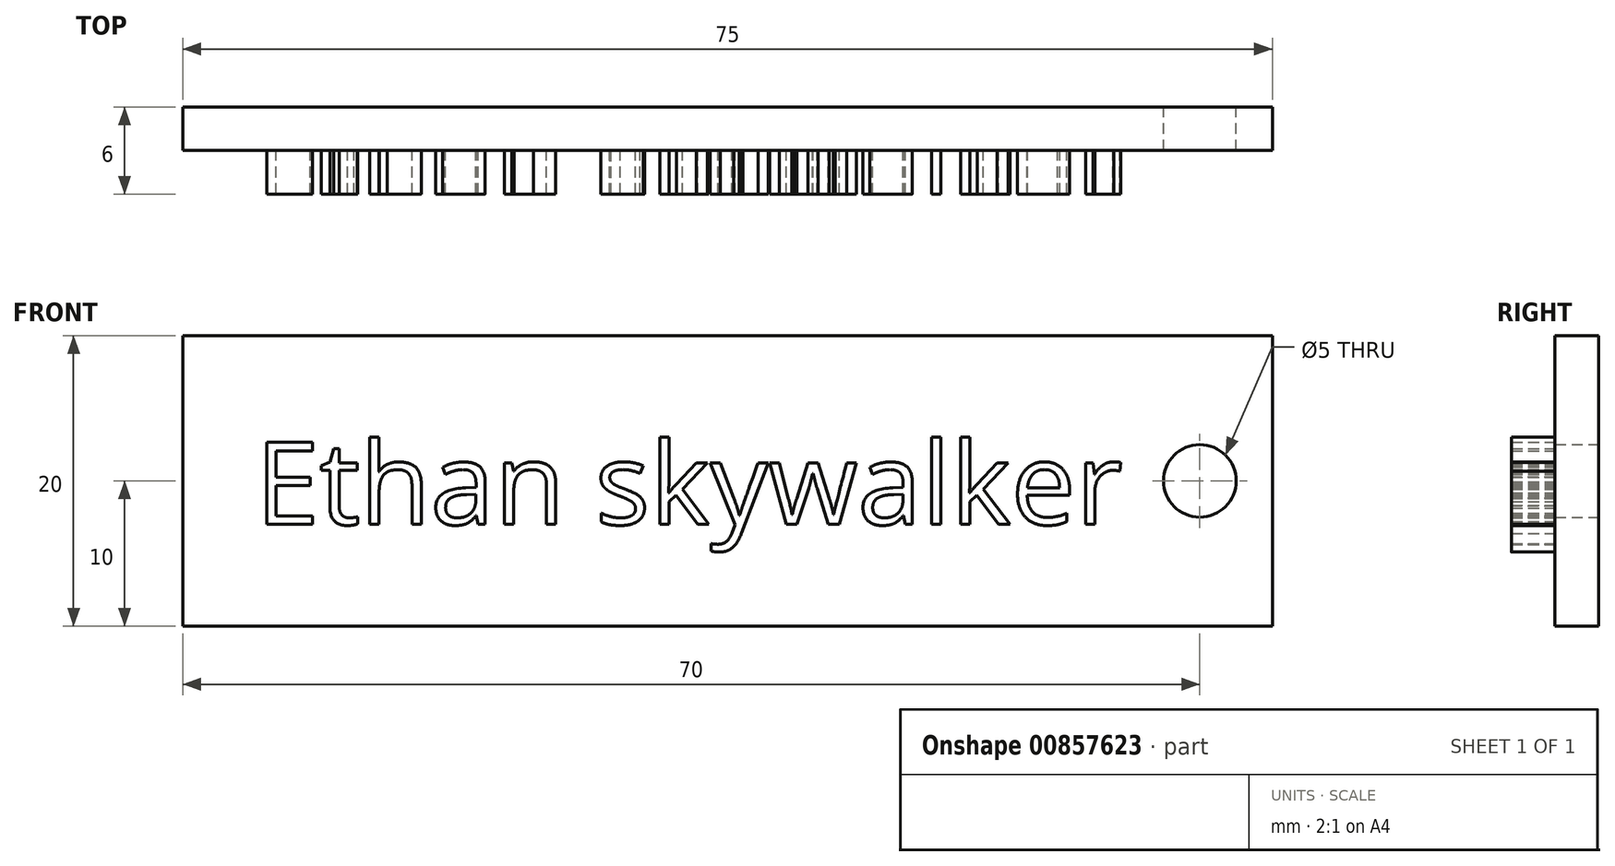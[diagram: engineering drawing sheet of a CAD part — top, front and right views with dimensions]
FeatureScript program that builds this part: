
annotation { "Feature Type Name" : "Feature", "Feature Type Description" : "" }
export const myFeature = defineFeature(function(context is Context, id is Id, definition is map)
    precondition{}
    {
        {
            var Q0;
            Q0=qCreatedBy(makeId("Front.planeOp"),FACE);
            var sketch = newSketch(context, id + "F0", { "sketchPlane" : qUnion([Q0])});
            skLineSegment(sketch, "E0.bottom", {"start": v(0, 0) * mm, "end": v(75, 0) * mm});
            skLineSegment(sketch, "E0.top", {"start": v(0, -20) * mm, "end": v(75, -20) * mm});
            skLineSegment(sketch, "E0.left", {"start": v(0, 0) * mm, "end": v(0, -20) * mm});
            skLineSegment(sketch, "E0.right", {"start": v(75, 0) * mm, "end": v(75, -20) * mm});
            skCircle(sketch, "E1", {"center": v(70, -10) * mm, "radius": 2.5 * mm});
            skSolve(sketch);
        }
        {
            var Q0;
            Q0=makeQuery(id+"F0.imprint","IMPRINT",FACE,{"disambiguationData":[TD([[makeQuery(id+"F0.imprint","IMPRINT",EDGE,{"derivedFrom":sQuery(id+"F0.wireOp",EDGE,"E0.bottom")}),-1.0]])]});
            extrude(context, id + "F1", {"entities" : qUnion([Q0]), "depth" : 3 * mm, "offsetDistance" : 25 * mm});
        }
        {
            var Q0;
            Q0=makeQuery(id+"F1.opExtrude","CAP_FACE",FACE,{"disambiguationData":[OSD([sQuery(id+"F0.wireOp",EDGE,"E0.bottom"),sQuery(id+"F0.wireOp",EDGE,"E0.top"),sQuery(id+"F0.wireOp",EDGE,"E0.left"),sQuery(id+"F0.wireOp",EDGE,"E0.right"),sQuery(id+"F0.wireOp",EDGE,"E1")])],"isStart":false});
            var sketch = newSketch(context, id + "F2", { "sketchPlane" : qUnion([Q0])});
            skText(sketch, "E2", { "text": "Ethan skywalker \n", "fontName": "OpenSans-Regular.ttf"});
            const initialGuessF2  = {"E2": [0.005, -0.013, 1, 0, 0.0057]};
            skSetInitialGuess(sketch, initialGuessF2);
            skSolve(sketch);
        }
        {
            var Q0;
            Q0 = qSketchRegion(id + "F2", true);
            extrude(context, id + "F3", {"entities" : qUnion([Q0]), "operationType" : NewBodyOperationType.ADD, "depth" : 3 * mm, "offsetDistance" : 25 * mm});
        }
    });
